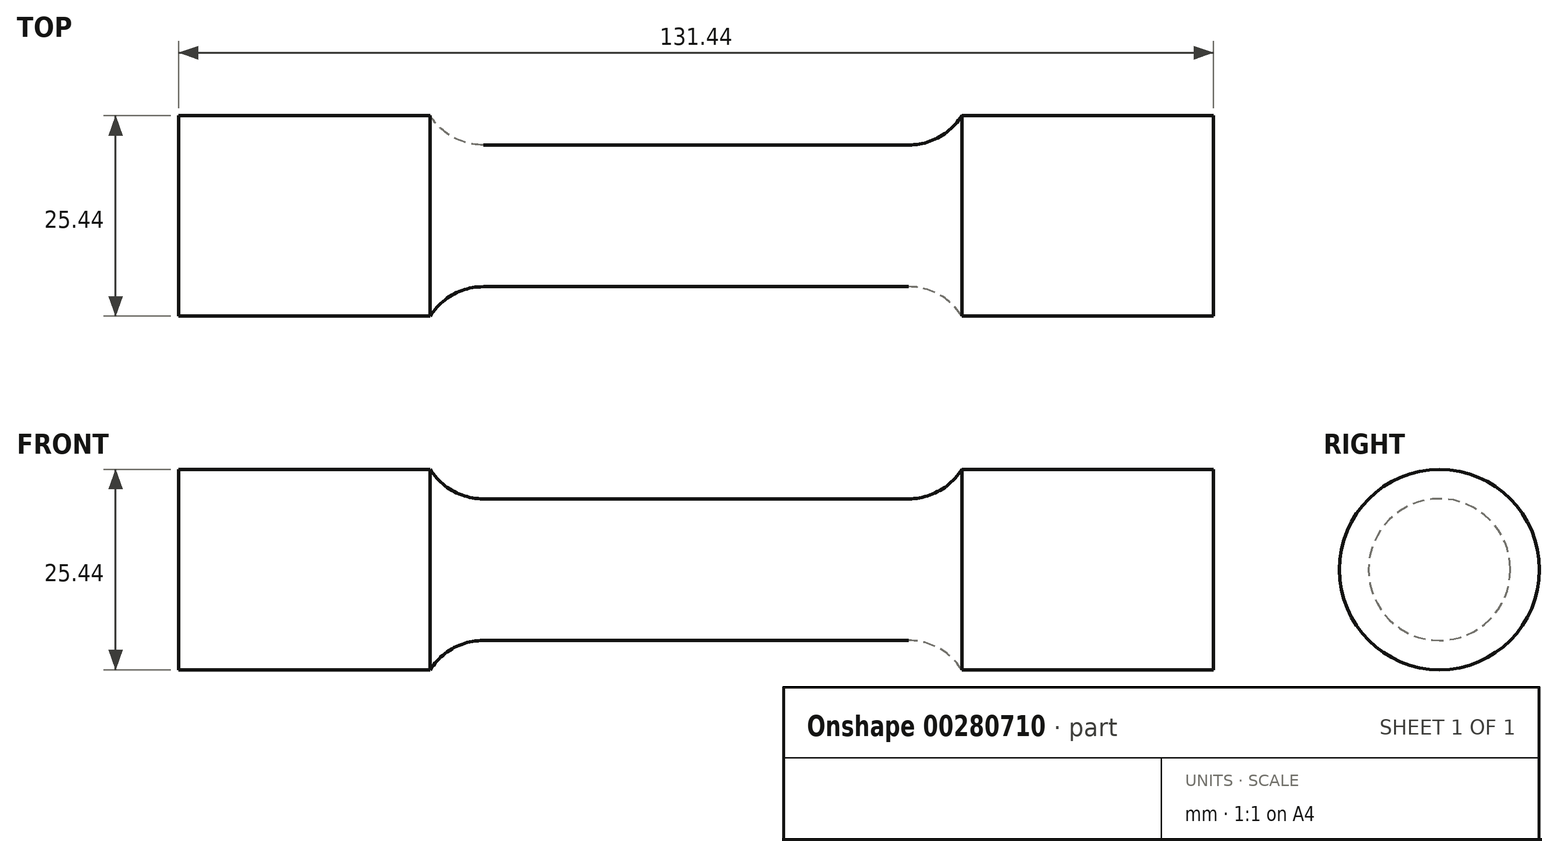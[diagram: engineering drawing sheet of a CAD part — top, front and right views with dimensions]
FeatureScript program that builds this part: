
annotation { "Feature Type Name" : "Feature", "Feature Type Description" : "" }
export const myFeature = defineFeature(function(context is Context, id is Id, definition is map)
    precondition{}
    {
        {
            var Q0;
            Q0=qCreatedBy(makeId("Front.planeOp"),FACE);
            var sketch = newSketch(context, id + "F0", { "sketchPlane" : qUnion([Q0])});
            skLineSegment(sketch, "E0", {"start": v(0, 9) * mm, "end": v(27, 9) * mm});
            skArc(sketch, "E1", {"start": v(27, 9) * mm, "mid": v(30.86, 10) * mm, "end": v(33.76, 12.72) * mm});
            skLineSegment(sketch, "E2", {"start": v(33.76, 12.72) * mm, "end": v(65.72, 12.72) * mm});
            skLineSegment(sketch, "E3", {"start": v(65.72, 12.72) * mm, "end": v(65.72, 0) * mm});
            skLineSegment(sketch, "E4.MirrorCS", {"start": v(0, 9) * mm, "end": v(-27, 9) * mm});
            skLineSegment(sketch, "E5.MirrorCS", {"start": v(-65.72, 12.72) * mm, "end": v(-65.72, 0) * mm});
            skLineSegment(sketch, "E6.MirrorCS", {"start": v(-33.76, 12.72) * mm, "end": v(-65.72, 12.72) * mm});
            skArc(sketch, "E7.MirrorCS", {"start": v(-27, 9) * mm, "mid": v(-30.86, 10) * mm, "end": v(-33.76, 12.72) * mm});
            skLineSegment(sketch, "E8", {"start": v(-65.72, 0) * mm, "end": v(65.72, 0) * mm});
            skSolve(sketch);
        }
        {
            var Q0;
            Q0 = qSketchRegion(id + "F0", true);
            var Q1;
            Q1=sQuery(id+"F0.wireOp",EDGE,"E8");
            revolve(context, id + "F1", {"entities" : qUnion([Q0]), "axis" : qUnion([Q1]), "revolveType" : RevolveType.FULL});
        }
    });
